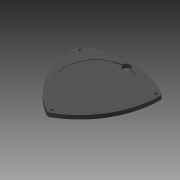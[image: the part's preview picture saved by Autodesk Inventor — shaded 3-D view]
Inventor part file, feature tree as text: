
AUTODESK INVENTOR PART (.ipt)
format: ipt  version: 2013 (Build 170138000, 138)  size: 130,048 bytes
history: native  units: mm
features: sketch x6, extrude x5, hole x1
ambient origin geometry x8: Origin, YZ Plane, XZ Plane, XY Plane, X Axis, Y Axis, Z Axis, Center Point
bodies: Solid1 (feature_tree)
feature tree (12):
  extrude  "Extrusion1"  Depth=250.0mm
  extrude  "Extrusion2"  Depth=12.5mm TaperAngle=0.0deg
  extrude  "Extrusion3"  Depth=5.0mm TaperAngle=0.0deg
  hole  "Hole1"  [1 undecoded]
  extrude  "Extrusion5"  Depth=37.5mm
  extrude  "Extrusion7"  Depth=25.0mm
  sketch  "Sketch1"  dims[d0=200.0mm d2=250.0mm]
  sketch  "Sketch2"  dims[d3=12.5mm d4=12.5mm d5=0.0mm]
  sketch  "Sketch3"  dims[d6=8.1mm d8=5.0mm d9=0.0mm]
  sketch  "Sketch5"  dims[d10=200.1mm d12=1.5mm d13=0.0mm]
  sketch  "Sketch7"  dims[d19=8.1mm d20=6.0mm d21=15.0mm d22=8.0mm d23=90.0deg d24=8.0mm d25=20.594885mm d30=37.5mm]
  sketch  "Sketch9"  dims[d33=2.0mm d34=0.0mm d39=25.0mm d41=10.0mm d42=0.0mm]
note: 1 required parameter value undecoded (feature->parameter linkage not recoverable at this tier; creation-order binding heuristic only, values carry confidence <= 0.55)
